# Revit family: Haworth_Planes_ConferenceTable_PebbleOnePiece
name_source: partatom
category: Furniture Systems
revit_build: Autodesk Revit 2018 (Build: 20170223_1515(x64)
units: mm (PartAtom-declared; Revit-internal decimal feet)

## family parameters
Always vertical = Yes
Cut with Voids When Loaded = No
OmniClass Number = 23.40.70.14.64.21
OmniClass Title = Systems Furniture
Part Type = Normal
Room Calculation Point = No
Round Connector Dimension = Use Diameter
Shared = No
Work Plane-Based = No

## types (1)
- 120w 60d
    Actual Depth = 60"
    Actual Height = 29"
    Actual Width = 120"
    Assembly Code = E2020200
    Cable Base = Yes
    Cable Base 14x14 = Yes
    Custom Size = No
    Cutout = Yes
    Cutout Depth = 4"
    Cutout Width = 8"
    Depth = 60"
    Description = Haworth - Planes Conference Table - Pebble One Piece
    Manufacturer = Haworth
    Max. Depth = 60"
    Max. Height = 29"
    Max. Width = 120"
    Middle Leg = No
    Middle Leg Off_Override = No
    Middle Leg_Interior = No
    Min. Depth = 36"
    Min. Height = 29"
    Min. Width = 84"
    Min/Max Width = 72-120 @ 6 in. increments
    Model = TARP
    Opening Center = Yes
    Opening Double = No
    Opening Double Wide = No
    Opening Single = Yes
    Opening Single Wide = No
    Revision Number = 3
    Size = Verify Final Dim. w/ Haworth
    Standard Depths = 36, 42, 48, 54, 60 in.
    Standard Height = 29 in.
    Support Height = 27 13/16"
    Support Location_Front_Back = 6"
    Support Location_Side = 10"
    Sustainability Info = https://www.haworth.com
    Table Thickness = 1 3/16"
    URL = www.haworth.com
    URL - Product = http://www.haworth.com
    Warranty = http://www.haworth.com
    Width = 120"

## geometry (parser evidence)
native form markers: Sweep x17
no freeform markers — native parametric forms only
